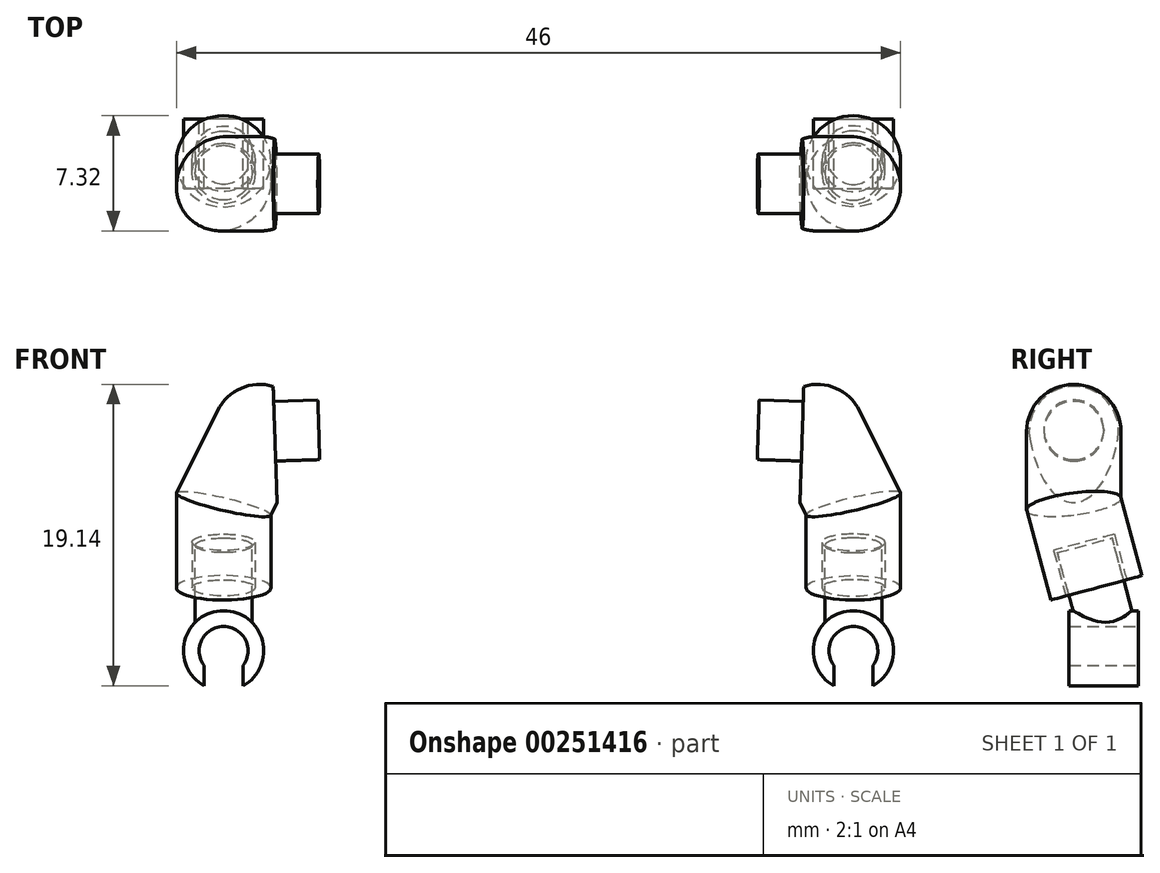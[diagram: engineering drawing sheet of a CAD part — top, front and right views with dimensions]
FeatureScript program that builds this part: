
annotation { "Feature Type Name" : "Feature", "Feature Type Description" : "" }
export const myFeature = defineFeature(function(context is Context, id is Id, definition is map)
    precondition{}
    {
        {
            var Q0;
            Q0=qCreatedBy(makeId("Front.planeOp"),FACE);
            var sketch = newSketch(context, id + "F0", { "sketchPlane" : qUnion([Q0])});
            skArc(sketch, "E0", {"start": v(1.25, -2.22) * mm, "mid": v(0, 2.55) * mm, "end": v(-1.25, -2.22) * mm});
            skArc(sketch, "E1", {"start": v(1.25, -0.92) * mm, "mid": v(0, 1.55) * mm, "end": v(-1.25, -0.92) * mm});
            skLineSegment(sketch, "E2", {"start": v(-1.25, -0.92) * mm, "end": v(-1.25, -2.22) * mm});
            skLineSegment(sketch, "E3", {"start": v(1.25, -0.92) * mm, "end": v(1.25, -2.22) * mm});
            skSolve(sketch);
        }
        {
            var Q0;
            Q0 = qSketchRegion(id + "F0", true);
            extrude(context, id + "F1", {"entities" : qUnion([Q0]), "depth" : 4.4 * mm});
        }
        {
            var Q0;
            Q0=qCreatedBy(makeId("Right.planeOp"),FACE);
            var sketch = newSketch(context, id + "F2", { "sketchPlane" : qUnion([Q0])});
            skLineSegment(sketch, "E4", {"start": v(-2.67, 4) * mm, "end": v(-4.1, 9.32) * mm});
            skLineSegment(sketch, "E5", {"start": v(0, 0) * mm, "end": v(-7.08, 0) * mm, "construction": true});
            skSolve(sketch);
        }
        {
            var Q0;
            Q0=sQuery(id+"F2.wireOp",VERTEX,"E4.end");
            var Q1;
            Q1=qCreatedBy(makeId("Front.planeOp"),FACE);
            cPlane(context, id + "F3", {"entities" : qUnion([Q0, Q1]), "cplaneType" : CPlaneType.PLANE_POINT, "offset" : 25 * mm, "width" : 150 * mm, "height" : 150 * mm});
        }
        {
            var Q0;
            Q0=qCreatedBy(id+"F3.planeOp",FACE);
            var sketch = newSketch(context, id + "F4", { "sketchPlane" : qUnion([Q0])});
            skLineSegment(sketch, "E6", {"start": v(0, 9.32) * mm, "end": v(2.3, 13.92) * mm});
            skSolve(sketch);
        }
        {
            var Q0;
            Q0=sQuery(id+"F4.wireOp",VERTEX,"E6.end");
            var Q1;
            Q1=sQuery(id+"F4.wireOp",EDGE,"E6");
            cPlane(context, id + "F5", {"entities" : qUnion([Q0, Q1]), "cplaneType" : CPlaneType.CURVE_POINT, "offset" : 25 * mm, "width" : 150 * mm, "height" : 150 * mm});
        }
        {
            var Q0;
            Q0=qCreatedBy(id+"F5.planeOp",FACE);
            var sketch = newSketch(context, id + "F6", { "sketchPlane" : qUnion([Q0])});
            skCircle(sketch, "E7", {"center": v(-4.17, -4.1) * mm, "radius": 3 * mm});
            skSolve(sketch);
        }
        {
            var Q0;
            Q0 = qSketchRegion(id + "F6", true);
            var Q1;
            Q1 = qConstructionFilter(qBodyType(qCreatedBy(id + "F2" ,EDGE), BodyType.WIRE), ConstructionObject.NO);
            var Q2;
            Q2=sQuery(id+"F4.wireOp",EDGE,"E6");
            sweep(context, id + "F7", {"operationType" : NewBodyOperationType.ADD, "profiles" : qUnion([Q0]), "path" : qUnion([Q1, Q2])});
        }
        {
            var Q0;
            Q0=makeQuery(id+"F7.opSweep","CAP_FACE",FACE,{"disambiguationData":[OSD([sQuery(id+"F2.wireOp",VERTEX,"U9vfRp8y-cp8L-0oOY-gu05-zVF7wjmpcWYL.end"),sQuery(id+"F6.wireOp",EDGE,"E7")])],"isStart":true});
            var sketch = newSketch(context, id + "F8", { "sketchPlane" : qUnion([Q0])});
            skArc(sketch, "E8.0", {"start": v(-7.17, -4.1) * mm, "mid": v(-4.17, -7.1) * mm, "end": v(-1.17, -4.1) * mm});
            skLineSegment(sketch, "E9", {"start": v(-7.17, -4.1) * mm, "end": v(-1.17, -4.1) * mm});
            skSolve(sketch);
        }
        {
            var Q0;
            Q0=makeQuery(id+"F8.imprint","IMPRINT",FACE,{"disambiguationData":[TD([[makeQuery(id+"F8.imprint","IMPRINT",EDGE,{"derivedFrom":sQuery(id+"F8.wireOp",EDGE,"E8.0")}),-1.0]])]});
            var Q1;
            Q1 = qConstructionFilter(qBodyType(qCreatedBy(id + "F8" ,EDGE), BodyType.WIRE), ConstructionObject.NO);
            var Q2;
            Q2=sQuery(id+"F8.wireOp",EDGE,"E9");
            revolve(context, id + "F9", {"operationType" : NewBodyOperationType.ADD, "entities" : qUnion([Q0]), "surfaceEntities" : qUnion([Q1]), "axis" : qUnion([Q2]), "revolveType" : RevolveType.FULL});
        }
        {
            var Q0;
            Q0=makeQuery(id+"F7.opSweep","CAP_FACE",FACE,{"disambiguationData":[OSD([sQuery(id+"F2.wireOp",VERTEX,"E4.start"),sQuery(id+"F6.wireOp",EDGE,"E7")])],"isStart":false});
            var sketch = newSketch(context, id + "F10", { "sketchPlane" : qUnion([Q0])});
            skCircle(sketch, "E10", {"center": v(0, 1.55) * mm, "radius": 2 * mm});
            skSolve(sketch);
        }
        {
            var Q0;
            Q0 = qSketchRegion(id + "F10", true);
            extrude(context, id + "F11", {"entities" : qUnion([Q0]), "operationType" : NewBodyOperationType.REMOVE, "oppositeDirection" : true, "depth" : 3 * mm});
        }
        {
            var Q0;
            Q0=makeQuery(id+"F11.boolean.opBoolean","COPY",FACE,{"derivedFrom":makeQuery(id+"F11.opExtrude","CAP_FACE",FACE,{"disambiguationData":[OSD([sQuery(id+"F10.wireOp",EDGE,"E10")])],"isStart":false})});
            cPlane(context, id + "F12", {"entities" : qUnion([Q0]), "cplaneType" : CPlaneType.OFFSET, "offset" : .2 * mm, "width" : 150 * mm, "height" : 150 * mm});
        }
        {
            var Q0;
            Q0=qCreatedBy(id+"F12.planeOp",FACE);
            var sketch = newSketch(context, id + "F13", { "sketchPlane" : qUnion([Q0])});
            skCircle(sketch, "E11.0", {"center": v(0, 1.55) * mm, "radius": 1.8 * mm});
            skSolve(sketch);
        }
        {
            var Q0;
            Q0 = qSketchRegion(id + "F13", true);
            var Q1;
            Q1=makeQuery(id+"F1.opExtrude","SWEPT_BODY",BODY,{"disambiguationData":[OSD([sQuery(id+"F0.wireOp",EDGE,"E0"),sQuery(id+"F0.wireOp",EDGE,"E1"),sQuery(id+"F0.wireOp",EDGE,"E2"),sQuery(id+"F0.wireOp",EDGE,"E3")])]});
            extrude(context, id + "F14", {"entities" : qUnion([Q0]), "operationType" : NewBodyOperationType.ADD, "endBound" : BoundingType.UP_TO_BODY, "endBoundEntityBody" : qUnion([Q1]), "depth" : 25 * mm});
        }
        {
            var Q0;
            Q0=qCreatedBy(makeId("Front.planeOp"),FACE);
            var sketch = newSketch(context, id + "F15", { "sketchPlane" : qUnion([Q0])});
            skLineSegment(sketch, "E12", {"start": v(0, 0) * mm, "end": v(25.95, 0) * mm, "construction": true});
            skLineSegment(sketch, "E13", {"start": v(14.39, 19.6) * mm, "end": v(3.14, 17.21) * mm});
            skLineSegment(sketch, "E14", {"start": v(3.14, 17.21) * mm, "end": v(3.6, 3) * mm});
            skLineSegment(sketch, "E15", {"start": v(3.6, 3) * mm, "end": v(19.74, 6.43) * mm});
            skLineSegment(sketch, "E16", {"start": v(19.74, 6.43) * mm, "end": v(14.39, 19.6) * mm});
            skLineSegment(sketch, "E17", {"start": v(8.76, 18.4) * mm, "end": v(11.67, 4.72) * mm, "construction": true});
            skPoint(sketch, "E17.endSnap0", {"position": v(11.67, 4.72) * mm});
            skSolve(sketch);
        }
        {
            var Q0;
            Q0=makeQuery(id+"F15.imprint","IMPRINT",FACE,{"disambiguationData":[TD([[makeQuery(id+"F15.imprint","IMPRINT",EDGE,{"derivedFrom":sQuery(id+"F15.wireOp",EDGE,"E13")}),1.0]])]});
            extrude(context, id + "F16", {"entities" : qUnion([Q0]), "operationType" : NewBodyOperationType.REMOVE, "depth" : 25 * mm});
        }
        {
            var Q0;
            Q0=makeQuery(id+"F16.boolean.opBoolean","COPY",FACE,{"derivedFrom":makeQuery(id+"F16.opExtrude","SWEPT_FACE",FACE,{"disambiguationData":[OSD([sQuery(id+"F15.wireOp",EDGE,"E14")])]})});
            var sketch = newSketch(context, id + "F17", { "sketchPlane" : qUnion([Q0])});
            skCircle(sketch, "E18", {"center": v(-4.1, 13.84) * mm, "radius": 1.9 * mm});
            skSolve(sketch);
        }
        {
            var Q0;
            Q0=makeQuery(id+"F17.imprint","IMPRINT",FACE,{"disambiguationData":[TD([[makeQuery(id+"F17.imprint","IMPRINT",EDGE,{"derivedFrom":sQuery(id+"F17.wireOp",EDGE,"E18")}),1.0]])]});
            extrude(context, id + "F18", {"entities" : qUnion([Q0]), "operationType" : NewBodyOperationType.ADD, "depth" : 2.8 * mm});
        }
        {
            var Q0;
            Q0=qCreatedBy(makeId("Right.planeOp"),FACE);
            cPlane(context, id + "F19", {"entities" : qUnion([Q0]), "cplaneType" : CPlaneType.OFFSET, "offset" : 20 * mm, "width" : 150 * mm, "height" : 150 * mm});
        }
        {
            var Q0;
            Q0=makeQuery(id+"F7.opSweep","SWEPT_BODY",BODY,{"disambiguationData":[OSD([sQuery(id+"F4.wireOp",EDGE,"E6"),sQuery(id+"F6.wireOp",EDGE,"E7")])]});
            var Q1;
            Q1=makeQuery(id+"F1.opExtrude","SWEPT_BODY",BODY,{"disambiguationData":[OSD([sQuery(id+"F0.wireOp",EDGE,"E0"),sQuery(id+"F0.wireOp",EDGE,"E1"),sQuery(id+"F0.wireOp",EDGE,"E2"),sQuery(id+"F0.wireOp",EDGE,"E3")])]});
            var Q2;
            Q2=qCreatedBy(id+"F19.planeOp",FACE);
            mirror(context, id + "F20", {"entities" : qUnion([Q0, Q1]), "mirrorPlane" : qUnion([Q2])});
        }
    });
